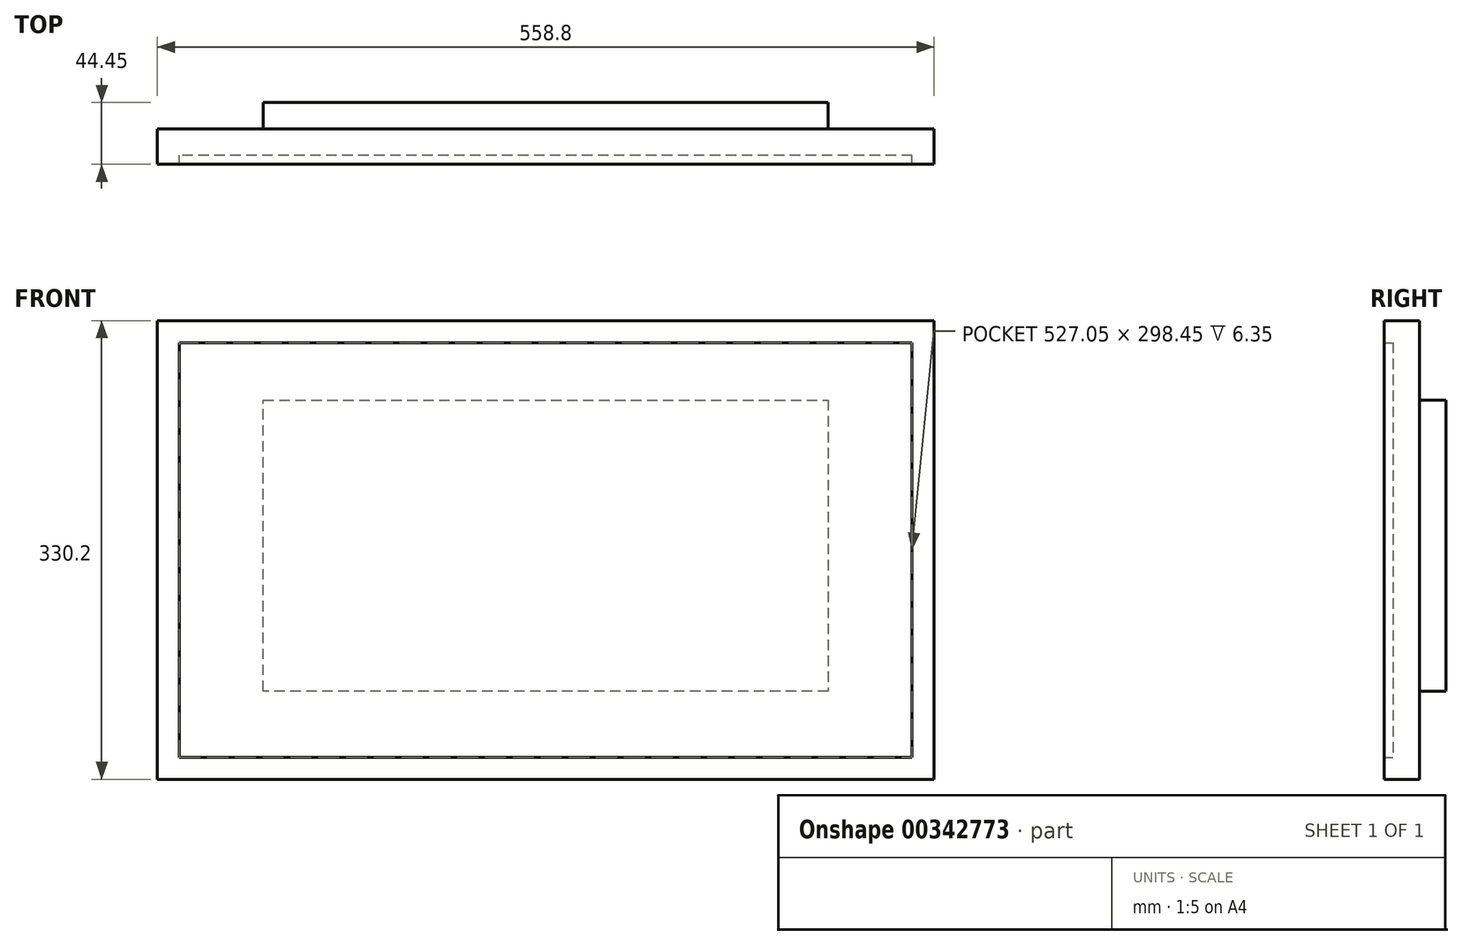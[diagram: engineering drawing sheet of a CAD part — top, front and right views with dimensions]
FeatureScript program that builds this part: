
annotation { "Feature Type Name" : "Feature", "Feature Type Description" : "" }
export const myFeature = defineFeature(function(context is Context, id is Id, definition is map)
    precondition{}
    {
        {
            var Q0;
            Q0=qCreatedBy(makeId("Front.planeOp"),FACE);
            var sketch = newSketch(context, id + "F0", { "sketchPlane" : qUnion([Q0])});
            skLineSegment(sketch, "E0.bottom", {"start": v(-289.1, 187.95) * mm, "end": v(269.7, 187.95) * mm});
            skLineSegment(sketch, "E0.top", {"start": v(-289.1, -142.25) * mm, "end": v(269.7, -142.25) * mm});
            skLineSegment(sketch, "E0.left", {"start": v(-289.1, 187.95) * mm, "end": v(-289.1, -142.25) * mm});
            skLineSegment(sketch, "E0.right", {"start": v(269.7, 187.95) * mm, "end": v(269.7, -142.25) * mm});
            skLineSegment(sketch, "E1", {"start": v(-273.23, 172.07) * mm, "end": v(-273.23, -126.38) * mm});
            skLineSegment(sketch, "E2", {"start": v(-273.23, -126.38) * mm, "end": v(253.82, -126.38) * mm});
            skLineSegment(sketch, "E3", {"start": v(253.82, -126.38) * mm, "end": v(253.82, 172.07) * mm});
            skLineSegment(sketch, "E4", {"start": v(253.82, 172.07) * mm, "end": v(-273.23, 172.07) * mm});
            skSolve(sketch);
        }
        {
            var Q0;
            Q0=makeQuery(id+"F0.imprint","IMPRINT",FACE,{"disambiguationData":[TD([[makeQuery(id+"F0.imprint","IMPRINT",EDGE,{"derivedFrom":sQuery(id+"F0.wireOp",EDGE,"E0.bottom")}),-1.0]])]});
            extrude(context, id + "F1", {"entities" : qUnion([Q0]), "depth" : 25.4 * mm});
        }
        {
            var Q0;
            Q0=makeQuery(id+"F0.imprint","IMPRINT",FACE,{"disambiguationData":[TD([[makeQuery(id+"F0.imprint","IMPRINT",EDGE,{"derivedFrom":sQuery(id+"F0.wireOp",EDGE,"E1")}),1.0]])]});
            extrude(context, id + "F2", {"entities" : qUnion([Q0]), "operationType" : NewBodyOperationType.ADD, "depth" : 19.05 * mm});
        }
        {
            var Q0;
            Q0=makeQuery(id+"F0.imprint","IMPRINT",FACE,{"disambiguationData":[TD([[makeQuery(id+"F0.imprint","IMPRINT",EDGE,{"derivedFrom":sQuery(id+"F0.wireOp",EDGE,"E1")}),1.0]])]});
            var sketch = newSketch(context, id + "F3", { "sketchPlane" : qUnion([Q0])});
            skLineSegment(sketch, "E5", {"start": v(-212.9, 130.8) * mm, "end": v(193.5, 130.8) * mm});
            skLineSegment(sketch, "E6", {"start": v(193.5, 130.8) * mm, "end": v(193.5, -78.75) * mm});
            skLineSegment(sketch, "E7", {"start": v(193.5, -78.75) * mm, "end": v(-212.9, -78.75) * mm});
            skLineSegment(sketch, "E8", {"start": v(-212.9, -78.75) * mm, "end": v(-212.9, 130.8) * mm});
            skSolve(sketch);
        }
        {
            var Q0;
            Q0=makeQuery(id+"F3.imprint","IMPRINT",FACE,{"disambiguationData":[TD([[makeQuery(id+"F3.imprint","IMPRINT",EDGE,{"derivedFrom":sQuery(id+"F3.wireOp",EDGE,"E5")}),-1.0]])]});
            extrude(context, id + "F4", {"entities" : qUnion([Q0]), "operationType" : NewBodyOperationType.ADD, "oppositeDirection" : true, "depth" : 19.05 * mm});
        }
    });
